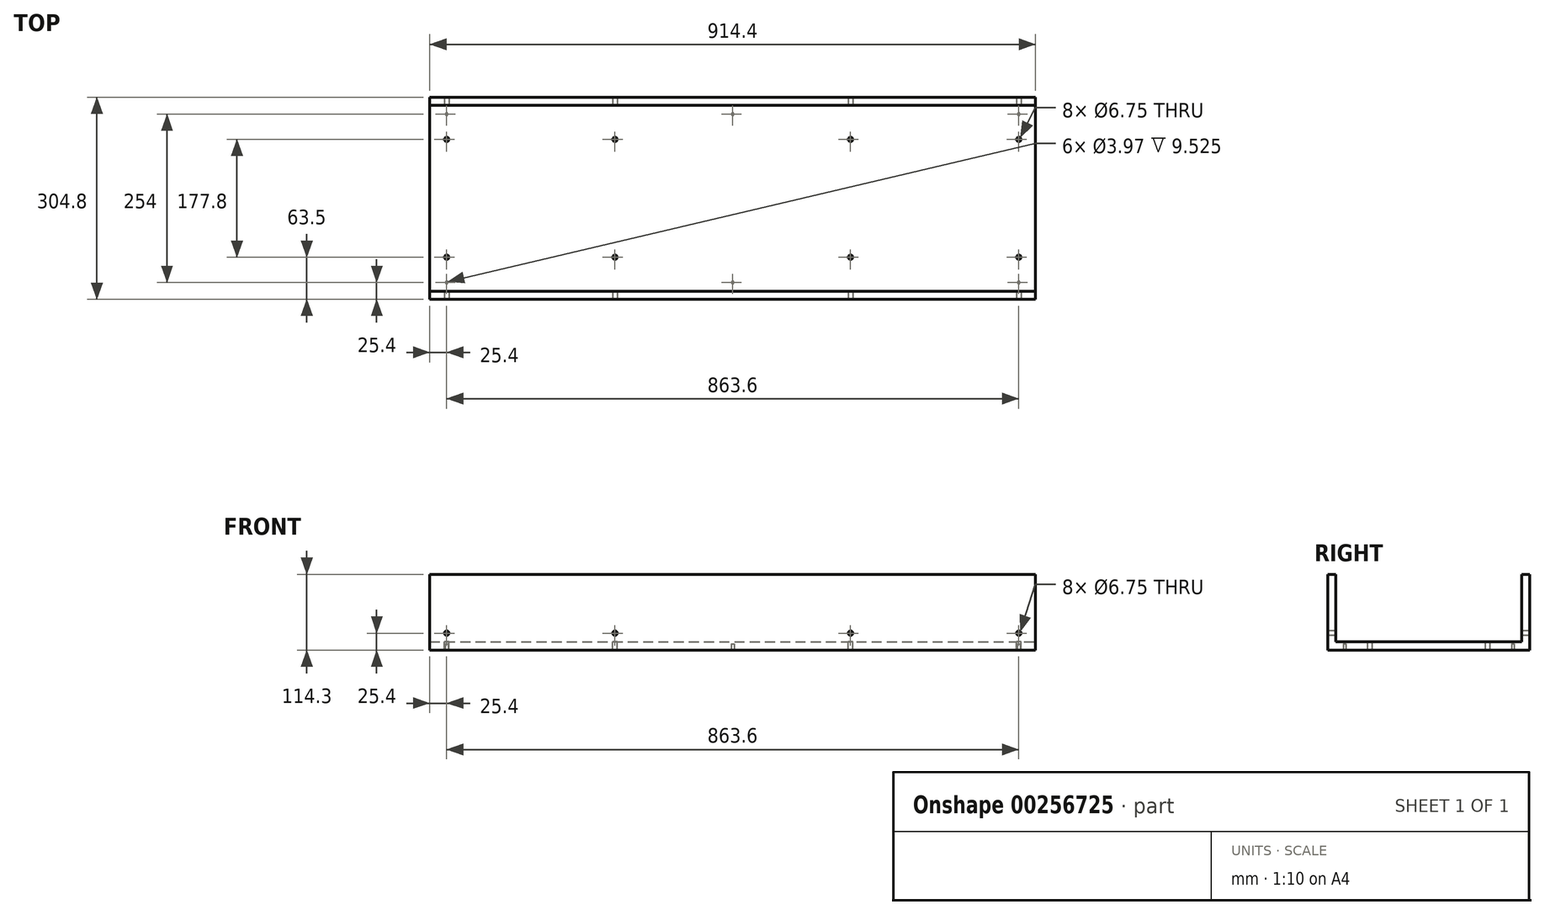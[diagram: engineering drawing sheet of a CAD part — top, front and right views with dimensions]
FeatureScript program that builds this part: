
annotation { "Feature Type Name" : "Feature", "Feature Type Description" : "" }
export const myFeature = defineFeature(function(context is Context, id is Id, definition is map)
    precondition{}
    {
        {
            var Q0;
            Q0=qCreatedBy(makeId("Top.planeOp"),FACE);
            var sketch = newSketch(context, id + "F0", { "sketchPlane" : qUnion([Q0])});
            skLineSegment(sketch, "E0.bottom", {"start": v(0, 0) * mm, "end": v(914.4, 0) * mm});
            skLineSegment(sketch, "E0.top", {"start": v(0, 304.8) * mm, "end": v(914.4, 304.8) * mm});
            skLineSegment(sketch, "E0.left", {"start": v(0, 0) * mm, "end": v(0, 304.8) * mm});
            skLineSegment(sketch, "E0.right", {"start": v(914.4, 0) * mm, "end": v(914.4, 304.8) * mm});
            skSolve(sketch);
        }
        {
            var Q0;
            Q0=makeQuery(id+"F0.imprint","IMPRINT",FACE,{"disambiguationData":[TD([[makeQuery(id+"F0.imprint","IMPRINT",EDGE,{"derivedFrom":sQuery(id+"F0.wireOp",EDGE,"E0.bottom")}),1.0]])]});
            extrude(context, id + "F1", {"entities" : qUnion([Q0]), "depth" : 12.7 * mm});
        }
        {
            var Q0;
            Q0=makeQuery(id+"F1.opExtrude","CAP_FACE",FACE,{"disambiguationData":[OSD([sQuery(id+"F0.wireOp",EDGE,"E0.bottom"),sQuery(id+"F0.wireOp",EDGE,"E0.top"),sQuery(id+"F0.wireOp",EDGE,"E0.left"),sQuery(id+"F0.wireOp",EDGE,"E0.right")])],"isStart":false});
            var sketch = newSketch(context, id + "F2", { "sketchPlane" : qUnion([Q0])});
            skLineSegment(sketch, "E1", {"start": v(0, 304.8) * mm, "end": v(914.4, 304.8) * mm});
            skLineSegment(sketch, "E2", {"start": v(0, 0) * mm, "end": v(914.4, 0) * mm});
            skLineSegment(sketch, "E3.0", {"start": v(0, 292.86) * mm, "end": v(914.4, 292.86) * mm});
            skLineSegment(sketch, "E4.0", {"start": v(0, 11.94) * mm, "end": v(914.4, 11.94) * mm});
            skSolve(sketch);
        }
        {
            var Q0;
            {var subQ0=sQuery(id+"F2.wireOp",EDGE,"E2");Q0=makeQuery(id+"F2.imprint","IMPRINT",FACE,{"disambiguationData":[TD([[makeQuery(id+"F2.imprint","IMPRINT",EDGE,{"derivedFrom":subQ0}),1.0]])]});}
            var Q1;
            {var subQ0=sQuery(id+"F2.wireOp",EDGE,"E1");Q1=makeQuery(id+"F2.imprint","IMPRINT",FACE,{"disambiguationData":[TD([[makeQuery(id+"F2.imprint","IMPRINT",EDGE,{"derivedFrom":subQ0}),-1.0]])]});}
            extrude(context, id + "F3", {"entities" : qUnion([Q0, Q1]), "operationType" : NewBodyOperationType.ADD, "depth" : 101.6 * mm});
        }
        {
            var Q0;
            Q0=makeQuery(id+"F1.opExtrude","CAP_FACE",FACE,{"disambiguationData":[OSD([sQuery(id+"F0.wireOp",EDGE,"E0.bottom"),sQuery(id+"F0.wireOp",EDGE,"E0.top"),sQuery(id+"F0.wireOp",EDGE,"E0.left"),sQuery(id+"F0.wireOp",EDGE,"E0.right")])],"isStart":false});
            var sketch = newSketch(context, id + "F4", { "sketchPlane" : qUnion([Q0])});
            skLineSegment(sketch, "E5.0", {"start": v(25.4, 11.94) * mm, "end": v(25.4, 292.86) * mm, "construction": true});
            skLineSegment(sketch, "E6.0", {"start": v(279.4, 11.94) * mm, "end": v(279.4, 292.86) * mm, "construction": true});
            skLineSegment(sketch, "E7", {"start": v(279.4, 152.4) * mm, "end": v(25.4, 152.4) * mm, "construction": true});
            skLineSegment(sketch, "E8.0", {"start": v(914.4, 241.3) * mm, "end": v(25.4, 241.3) * mm, "construction": true});
            skLineSegment(sketch, "E9.0", {"start": v(914.4, 63.5) * mm, "end": v(25.4, 63.5) * mm, "construction": true});
            skCircle(sketch, "E10", {"center": v(25.4, 241.3) * mm, "radius": 3.37 * mm});
            skCircle(sketch, "E11", {"center": v(279.4, 241.3) * mm, "radius": 3.37 * mm});
            skCircle(sketch, "E12", {"center": v(279.4, 63.5) * mm, "radius": 3.37 * mm});
            skLineSegment(sketch, "E13", {"start": v(914.4, 292.86) * mm, "end": v(914.4, 11.94) * mm, "construction": true});
            skLineSegment(sketch, "E14.0", {"start": v(889, 292.86) * mm, "end": v(889, 11.94) * mm, "construction": true});
            skLineSegment(sketch, "E15.0", {"start": v(635, 292.86) * mm, "end": v(635, 11.94) * mm, "construction": true});
            skCircle(sketch, "E16", {"center": v(635, 241.3) * mm, "radius": 3.37 * mm});
            skCircle(sketch, "E17", {"center": v(889, 241.3) * mm, "radius": 3.37 * mm});
            skCircle(sketch, "E18", {"center": v(635, 63.5) * mm, "radius": 3.37 * mm});
            skCircle(sketch, "E19", {"center": v(889, 63.5) * mm, "radius": 3.37 * mm});
            skCircle(sketch, "E20", {"center": v(25.4, 63.5) * mm, "radius": 3.37 * mm});
            skSolve(sketch);
        }
        {
            var Q0;
            Q0 = qSketchRegion(id + "F4", true);
            extrude(context, id + "F5", {"entities" : qUnion([Q0]), "operationType" : NewBodyOperationType.REMOVE, "oppositeDirection" : true, "depth" : 25.4 * mm});
        }
        {
            var Q0;
            Q0=makeQuery(id+"F3.opExtrude","SWEPT_FACE",FACE,{"disambiguationData":[OSD([sQuery(id+"F2.wireOp",EDGE,"E4.0")])]});
            var sketch = newSketch(context, id + "F6", { "sketchPlane" : qUnion([Q0])});
            skLineSegment(sketch, "E21.0", {"start": v(0, 25.4) * mm, "end": v(-914.4, 25.4) * mm, "construction": true});
            skLineSegment(sketch, "E22", {"start": v(0, 12.7) * mm, "end": v(0, 165.31) * mm, "construction": true});
            skLineSegment(sketch, "E23.0", {"start": v(-25.4, 12.7) * mm, "end": v(-25.4, 165.31) * mm, "construction": true});
            skLineSegment(sketch, "E24.0", {"start": v(-279.4, 12.7) * mm, "end": v(-279.4, 165.31) * mm, "construction": true});
            skLineSegment(sketch, "E25", {"start": v(-914.4, 12.7) * mm, "end": v(-914.4, 155.01) * mm, "construction": true});
            skLineSegment(sketch, "E26.0", {"start": v(-889, 12.7) * mm, "end": v(-889, 155.01) * mm, "construction": true});
            skLineSegment(sketch, "E27.0", {"start": v(-635, 12.7) * mm, "end": v(-635, 155.01) * mm, "construction": true});
            skCircle(sketch, "E28", {"center": v(-889, 25.4) * mm, "radius": 3.37 * mm});
            skCircle(sketch, "E29", {"center": v(-635, 25.4) * mm, "radius": 3.37 * mm});
            skCircle(sketch, "E30", {"center": v(-279.4, 25.4) * mm, "radius": 3.37 * mm});
            skCircle(sketch, "E31", {"center": v(-25.4, 25.4) * mm, "radius": 3.37 * mm});
            skSolve(sketch);
        }
        {
            var Q0;
            Q0 = qSketchRegion(id + "F6", true);
            extrude(context, id + "F7", {"entities" : qUnion([Q0]), "operationType" : NewBodyOperationType.REMOVE, "depth" : 655.32 * mm, "symmetric" : true});
        }
        {
            var Q0;
            Q0=makeQuery(id+"F1.opExtrude","CAP_FACE",FACE,{"disambiguationData":[OSD([sQuery(id+"F0.wireOp",EDGE,"E0.bottom"),sQuery(id+"F0.wireOp",EDGE,"E0.top"),sQuery(id+"F0.wireOp",EDGE,"E0.left"),sQuery(id+"F0.wireOp",EDGE,"E0.right")])],"isStart":true});
            var sketch = newSketch(context, id + "F8", { "sketchPlane" : qUnion([Q0])});
            skLineSegment(sketch, "E32.0", {"start": v(0, -279.4) * mm, "end": v(914.4, -279.4) * mm, "construction": true});
            skLineSegment(sketch, "E33.0", {"start": v(25.4, 0) * mm, "end": v(25.4, -304.8) * mm, "construction": true});
            skCircle(sketch, "E34", {"center": v(25.4, -279.4) * mm, "radius": 1.98 * mm});
            skLineSegment(sketch, "E35.0", {"start": v(889, 0) * mm, "end": v(889, -304.8) * mm, "construction": true});
            skCircle(sketch, "E36", {"center": v(889, -279.4) * mm, "radius": 1.98 * mm});
            skCircle(sketch, "E37", {"center": v(457.2, -279.4) * mm, "radius": 1.98 * mm});
            skCircle(sketch, "E38.0.1.0", {"center": v(889, -25.4) * mm, "radius": 1.98 * mm});
            skCircle(sketch, "E38.0.1.1", {"center": v(457.2, -25.4) * mm, "radius": 1.98 * mm});
            skCircle(sketch, "E38.0.1.2", {"center": v(25.4, -25.4) * mm, "radius": 1.98 * mm});
            skLineSegment(sketch, "E38.direction1", {"start": v(889, -279.4) * mm, "end": v(914.4, -279.4) * mm, "construction": true});
            skLineSegment(sketch, "E38.direction2", {"start": v(889, -279.4) * mm, "end": v(889, -25.4) * mm, "construction": true});
            skSolve(sketch);
        }
        {
            var Q0;
            Q0 = qSketchRegion(id + "F8", true);
            extrude(context, id + "F9", {"entities" : qUnion([Q0]), "operationType" : NewBodyOperationType.REMOVE, "oppositeDirection" : true, "depth" : 9.52 * mm});
        }
    });
